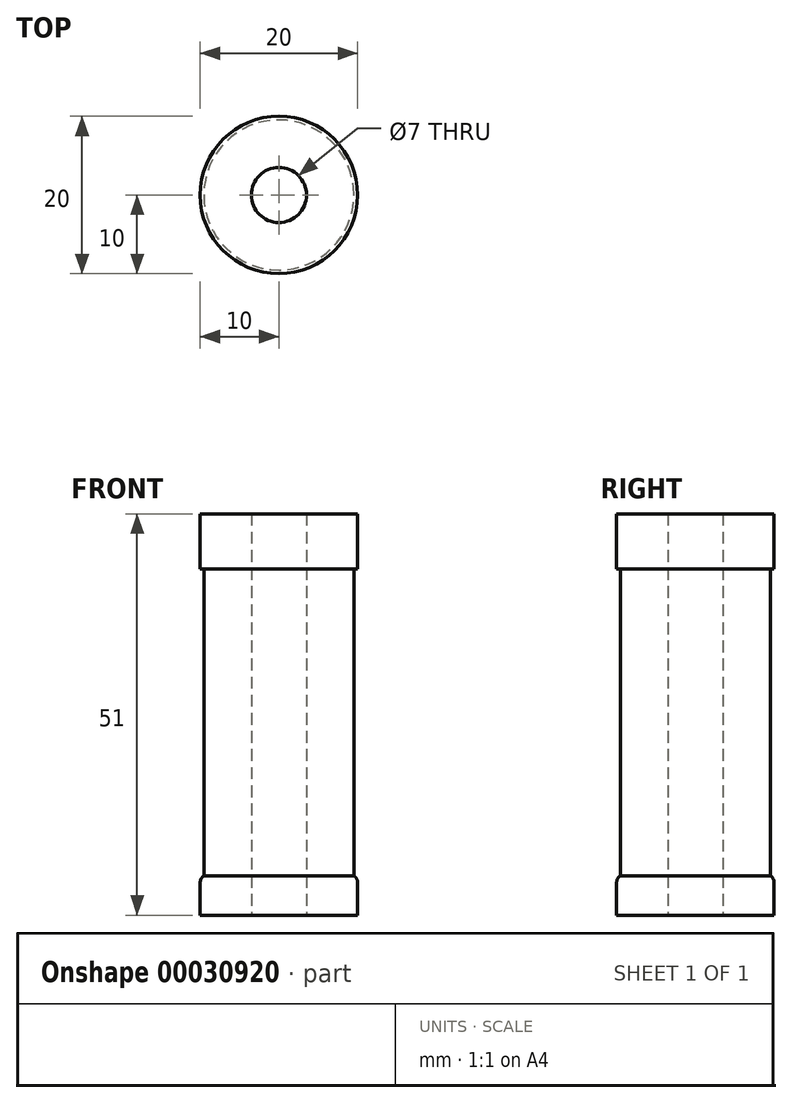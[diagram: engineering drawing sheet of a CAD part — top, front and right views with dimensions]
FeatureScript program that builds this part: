
annotation { "Feature Type Name" : "Feature", "Feature Type Description" : "" }
export const myFeature = defineFeature(function(context is Context, id is Id, definition is map)
    precondition{}
    {
        {
            var Q0;
            Q0=qCreatedBy(makeId("Top.planeOp"),FACE);
            var sketch = newSketch(context, id + "F0", { "sketchPlane" : qUnion([Q0])});
            skCircle(sketch, "E0", {"center": v(0, 0) * mm, "radius": 10 * mm});
            skCircle(sketch, "E1", {"center": v(0, 0) * mm, "radius": 3.5 * mm});
            skCircle(sketch, "E2", {"center": v(0, 0) * mm, "radius": 9.54 * mm});
            skCircle(sketch, "E3", {"center": v(0, 0) * mm, "radius": 4.5 * mm});
            skSolve(sketch);
        }
        {
            var Q0;
            Q0=makeQuery(id+"F0.imprint","IMPRINT",FACE,{"disambiguationData":[TD([[makeQuery(id+"F0.imprint","IMPRINT",EDGE,{"derivedFrom":sQuery(id+"F0.wireOp",EDGE,"E0")}),1.0]])]});
            var Q1;
            Q1=makeQuery(id+"F0.imprint","IMPRINT",FACE,{"disambiguationData":[TD([[makeQuery(id+"F0.imprint","IMPRINT",EDGE,{"derivedFrom":sQuery(id+"F0.wireOp",EDGE,"E2")}),1.0]])]});
            extrude(context, id + "F1", {"entities" : qUnion([Q0, Q1]), "depth" : 5 * mm});
        }
        {
            var Q0;
            Q0=makeQuery(id+"F0.imprint","IMPRINT",FACE,{"disambiguationData":[TD([[makeQuery(id+"F0.imprint","IMPRINT",EDGE,{"derivedFrom":sQuery(id+"F0.wireOp",EDGE,"E2")}),1.0]])]});
            extrude(context, id + "F2", {"entities" : qUnion([Q0]), "depth" : 44 * mm});
        }
        {
            var Q0;
            Q0=makeQuery(id+"F0.imprint","IMPRINT",FACE,{"disambiguationData":[TD([[makeQuery(id+"F0.imprint","IMPRINT",EDGE,{"derivedFrom":sQuery(id+"F0.wireOp",EDGE,"E1")}),-1.0]])]});
            extrude(context, id + "F3", {"entities" : qUnion([Q0]), "operationType" : NewBodyOperationType.ADD, "depth" : 51 * mm});
        }
        {
            var Q0;
            Q0=makeQuery(id+"F2.opExtrude","CAP_FACE",FACE,{"disambiguationData":[OSD([sQuery(id+"F0.wireOp",EDGE,"E2"),sQuery(id+"F0.wireOp",EDGE,"E3")])],"isStart":false});
            var sketch = newSketch(context, id + "F4", { "sketchPlane" : qUnion([Q0])});
            skCircle(sketch, "E4", {"center": v(0, 0) * mm, "radius": 4.5 * mm});
            skCircle(sketch, "E5", {"center": v(0, 0) * mm, "radius": 10 * mm});
            skSolve(sketch);
        }
        {
            var Q0;
            Q0=makeQuery(id+"F4.imprint","IMPRINT",FACE,{"disambiguationData":[TD([[makeQuery(id+"F4.imprint","IMPRINT",EDGE,{"derivedFrom":sQuery(id+"F4.wireOp",EDGE,"E4")}),-1.0]])]});
            var Q1;
            Q1=makeQuery(id+"F4.imprint","IMPRINT",FACE,{"disambiguationData":[TD([[makeQuery(id+"F4.imprint","IMPRINT",EDGE,{"derivedFrom":sQuery(id+"F4.wireOp",EDGE,"E5")}),1.0]])]});
            var Q2;
            Q2=makeQuery(id+"F3.opExtrude","CAP_FACE",FACE,{"disambiguationData":[OSD([sQuery(id+"F0.wireOp",EDGE,"E1"),sQuery(id+"F0.wireOp",EDGE,"E3")])],"isStart":false});
            extrude(context, id + "F5", {"entities" : qUnion([Q0, Q1]), "operationType" : NewBodyOperationType.ADD, "endBound" : BoundingType.UP_TO_SURFACE, "endBoundEntityFace" : qUnion([Q2]), "depth" : 6.11 * mm});
        }
        {
            var Q0;
            Q0=makeQuery(id+"F1.opExtrude","CAP_EDGE",EDGE,{"disambiguationData":[OSD([sQuery(id+"F0.wireOp",EDGE,"E0")])],"isStart":false});
            fillet(context, id + "F6", {"entities" : qUnion([Q0]), "radius" : 1 * mm, "tangentPropagation" : true, "allowEdgeOverflow" : false});
        }
    });
